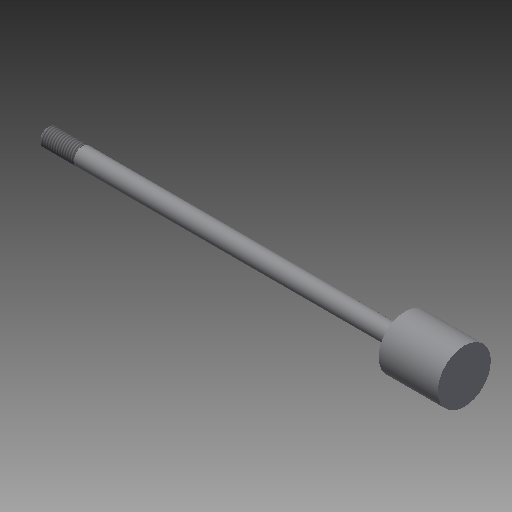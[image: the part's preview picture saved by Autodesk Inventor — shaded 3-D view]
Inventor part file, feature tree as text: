
AUTODESK INVENTOR PART (.ipt)
format: ipt  version: 2019 (Build 230136000, 136)  size: 155,648 bytes
history: native  units: in
note: dims shown in document units (in); Inventor stores cm internally (conversion verified against a paired STEP export)
features: other x84, revolve x3, sketch x3, thread x1
ambient origin geometry x8: Origin, YZ Plane, XZ Plane, XY Plane, X Axis, Y Axis, Z Axis, Center Point
bodies: Solid1 (feature_tree)
feature tree (91):
  revolve  "Revolution1"  Angle=360.0deg
  revolve  "Revolution2"  Angle=360.0deg
  thread  "Thread1"  [1 undecoded]
  revolve  "Revolution3"  [1 undecoded]
  other  "dia1_XY"
  other  "dia1_YZ"
  other  "dia1_ZX"
  other  "dia1_X"
  other  "dia1_Y"
  other  "dia1_Z"
  other  "dia1_Center"
  other  "dia12_XY"
  other  "dia12_YZ"
  other  "dia12_ZX"
  other  "dia12_X"
  other  "dia12_Y"
  other  "dia12_Z"
  other  "dia12_Center"
  other  "dia2_XY"
  other  "dia2_YZ"
  other  "dia2_ZX"
  other  "dia2_X"
  other  "dia2_Y"
  other  "dia2_Z"
  other  "dia2_Center"
  other  "dia22_XY"
  other  "dia22_YZ"
  other  "dia22_ZX"
  other  "dia22_X"
  other  "dia22_Y"
  other  "dia22_Z"
  other  "dia22_Center"
  other  "hh1_XY"
  other  "hh1_YZ"
  other  "hh1_ZX"
  other  "hh1_X"
  other  "hh1_Y"
  other  "hh1_Z"
  other  "hh1_Center"
  other  "hh2_XY"
  other  "hh2_YZ"
  other  "hh2_ZX"
  other  "hh2_X"
  other  "hh2_Y"
  other  "hh2_Z"
  other  "hh2_Center"
  other  "rl1_XY"
  other  "rl1_YZ"
  other  "rl1_ZX"
  other  "rl1_X"
  other  "rl1_Y"
  other  "rl1_Z"
  other  "rl1_Center"
  other  "rl2_XY"
  other  "rl2_YZ"
  other  "rl2_ZX"
  other  "rl2_X"
  other  "rl2_Y"
  other  "rl2_Z"
  other  "rl2_Center"
  other  "rod_cp_XY"
  other  "rod_cp_YZ"
  other  "rod_cp_ZX"
  other  "rod_cp_X"
  other  "rod_cp_Y"
  other  "rod_cp_Z"
  other  "rod_cp_Center"
  other  "thd1_XY"
  other  "thd1_YZ"
  other  "thd1_ZX"
  other  "thd1_X"
  other  "thd1_Y"
  other  "thd1_Z"
  other  "thd1_Center"
  other  "thd2_XY"
  other  "thd2_YZ"
  other  "thd2_ZX"
  other  "thd2_X"
  other  "thd2_Y"
  other  "thd2_Z"
  other  "thd2_Center"
  other  "to_rod_clevis_XY"
  other  "to_rod_clevis_YZ"
  other  "to_rod_clevis_ZX"
  other  "to_rod_clevis_X"
  other  "to_rod_clevis_Y"
  other  "to_rod_clevis_Z"
  other  "to_rod_clevis_Center"
  sketch  "Sketch_1"  dims[d0=360.0deg d1=360.0deg]
  sketch  "Sketch_3"  dims[d2=0.4787in d3=0.0in d4=360.0deg]
  sketch  "Sketch_30"  dims[d5=0.0in d6=0.0in d7=0.0in d8=0.0in d9=0.0in]
note: 2 required parameter values undecoded (feature->parameter linkage not recoverable at this tier; creation-order binding heuristic only, values carry confidence <= 0.55)
